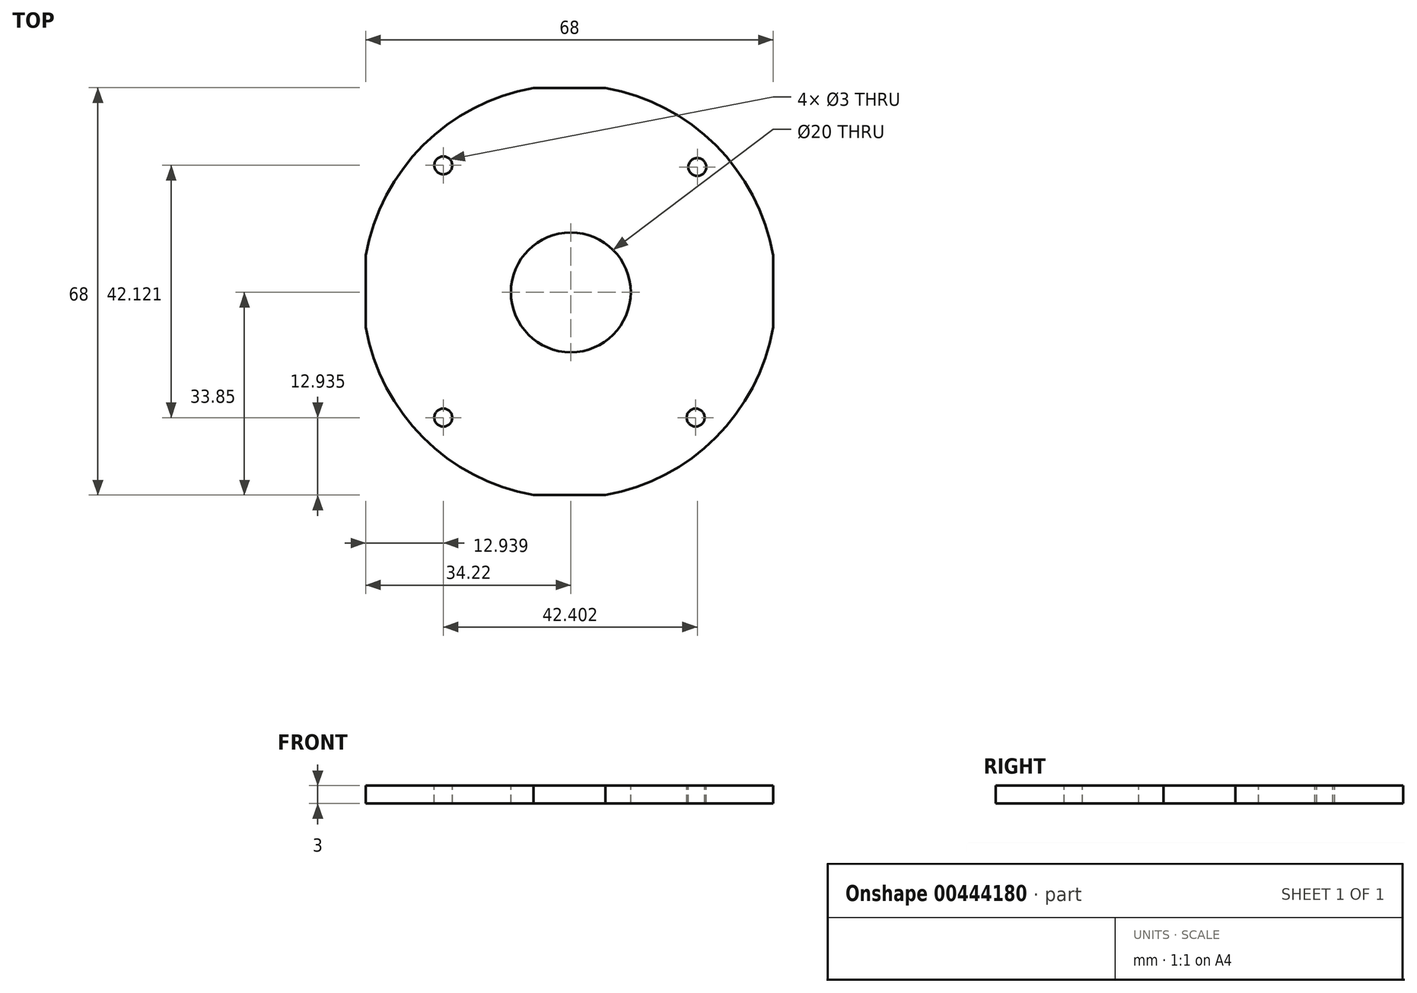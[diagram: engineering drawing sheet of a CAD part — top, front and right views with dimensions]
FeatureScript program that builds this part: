
annotation { "Feature Type Name" : "Feature", "Feature Type Description" : "" }
export const myFeature = defineFeature(function(context is Context, id is Id, definition is map)
    precondition{}
    {
        {
            var Q0;
            Q0=qCreatedBy(makeId("Top.planeOp"),FACE);
            var sketch = newSketch(context, id + "F0", { "sketchPlane" : qUnion([Q0])});
            skLineSegment(sketch, "E0.bottom", {"start": v(-6.22, 34.15) * mm, "end": v(5.78, 34.15) * mm});
            skLineSegment(sketch, "E0.top", {"start": v(-6.22, -33.85) * mm, "end": v(5.78, -33.85) * mm});
            skLineSegment(sketch, "E1.left", {"start": v(-34.22, 6.15) * mm, "end": v(-34.22, -5.85) * mm});
            skLineSegment(sketch, "E1.right", {"start": v(33.78, 6.15) * mm, "end": v(33.78, -5.85) * mm});
            skArc(sketch, "E2", {"start": v(-34.22, -5.85) * mm, "mid": v(-24.63, -24.27) * mm, "end": v(-6.22, -33.85) * mm});
            skArc(sketch, "E3.trimOffspring", {"start": v(33.78, 6.15) * mm, "mid": v(24.2, 24.56) * mm, "end": v(5.78, 34.15) * mm});
            skArc(sketch, "E4.trimOffspring", {"start": v(-6.22, 34.15) * mm, "mid": v(-24.63, 24.56) * mm, "end": v(-34.22, 6.15) * mm});
            skArc(sketch, "E5.trimOffspring", {"start": v(5.78, -33.85) * mm, "mid": v(24.2, -24.27) * mm, "end": v(33.78, -5.85) * mm});
            skSolve(sketch);
        }
        {
            var Q0;
            Q0=makeQuery(id+"F0.imprint","IMPRINT",FACE,{"disambiguationData":[TD([[makeQuery(id+"F0.imprint","IMPRINT",EDGE,{"derivedFrom":sQuery(id+"F0.wireOp",EDGE,"E0.bottom")}),-1.0]])]});
            extrude(context, id + "F1", {"entities" : qUnion([Q0]), "depth" : 3 * mm});
        }
        {
            var Q0;
            Q0=makeQuery(id+"F1.opExtrude","CAP_FACE",FACE,{"disambiguationData":[OSD([sQuery(id+"F0.wireOp",EDGE,"E0.bottom"),sQuery(id+"F0.wireOp",EDGE,"E0.top"),sQuery(id+"F0.wireOp",EDGE,"E1.left"),sQuery(id+"F0.wireOp",EDGE,"E1.right"),sQuery(id+"F0.wireOp",EDGE,"E2"),sQuery(id+"F0.wireOp",EDGE,"E3.trimOffspring"),sQuery(id+"F0.wireOp",EDGE,"E4.trimOffspring"),sQuery(id+"F0.wireOp",EDGE,"E5.trimOffspring")])],"isStart":false});
            var sketch = newSketch(context, id + "F2", { "sketchPlane" : qUnion([Q0])});
            skCircle(sketch, "E6", {"center": v(21.12, 20.93) * mm, "radius": 1.5 * mm});
            skCircle(sketch, "E7", {"center": v(-21.28, 21.2) * mm, "radius": 1.5 * mm});
            skCircle(sketch, "E8", {"center": v(-21.28, -20.91) * mm, "radius": 1.5 * mm});
            skCircle(sketch, "E9", {"center": v(20.84, -20.91) * mm, "radius": 1.5 * mm});
            skPoint(sketch, "E10.left.start.orphan", {"position": v(33.78, 6.15) * mm});
            skPoint(sketch, "E11.orphan", {"position": v(33.78, -5.85) * mm});
            skPoint(sketch, "E12.bottom.start.orphan", {"position": v(5.78, -33.85) * mm});
            skPoint(sketch, "E13.top.end.orphan", {"position": v(-6.22, -33.85) * mm});
            skCircle(sketch, "E14", {"center": v(0, 0) * mm, "radius": 10 * mm});
            skSolve(sketch);
        }
        {
            var Q0;
            Q0=makeQuery(id+"F2.imprint","IMPRINT",FACE,{"disambiguationData":[TD([[makeQuery(id+"F2.imprint","IMPRINT",EDGE,{"derivedFrom":sQuery(id+"F2.wireOp",EDGE,"E6")}),1.0]])]});
            var Q1;
            Q1=makeQuery(id+"F2.imprint","IMPRINT",FACE,{"disambiguationData":[TD([[makeQuery(id+"F2.imprint","IMPRINT",EDGE,{"derivedFrom":sQuery(id+"F2.wireOp",EDGE,"E7")}),1.0]])]});
            var Q2;
            Q2=makeQuery(id+"F2.imprint","IMPRINT",FACE,{"disambiguationData":[TD([[makeQuery(id+"F2.imprint","IMPRINT",EDGE,{"derivedFrom":sQuery(id+"F2.wireOp",EDGE,"E8")}),1.0]])]});
            var Q3;
            Q3=makeQuery(id+"F2.imprint","IMPRINT",FACE,{"disambiguationData":[TD([[makeQuery(id+"F2.imprint","IMPRINT",EDGE,{"derivedFrom":sQuery(id+"F2.wireOp",EDGE,"E9")}),1.0]])]});
            var Q4;
            Q4=makeQuery(id+"F2.imprint","IMPRINT",FACE,{"disambiguationData":[TD([[makeQuery(id+"F2.imprint","IMPRINT",EDGE,{"derivedFrom":sQuery(id+"F2.wireOp",EDGE,"E14")}),1.0]])]});
            extrude(context, id + "F3", {"entities" : qUnion([Q0, Q1, Q2, Q3, Q4]), "operationType" : NewBodyOperationType.REMOVE, "oppositeDirection" : true, "depth" : 25.4 * mm});
        }
    });
